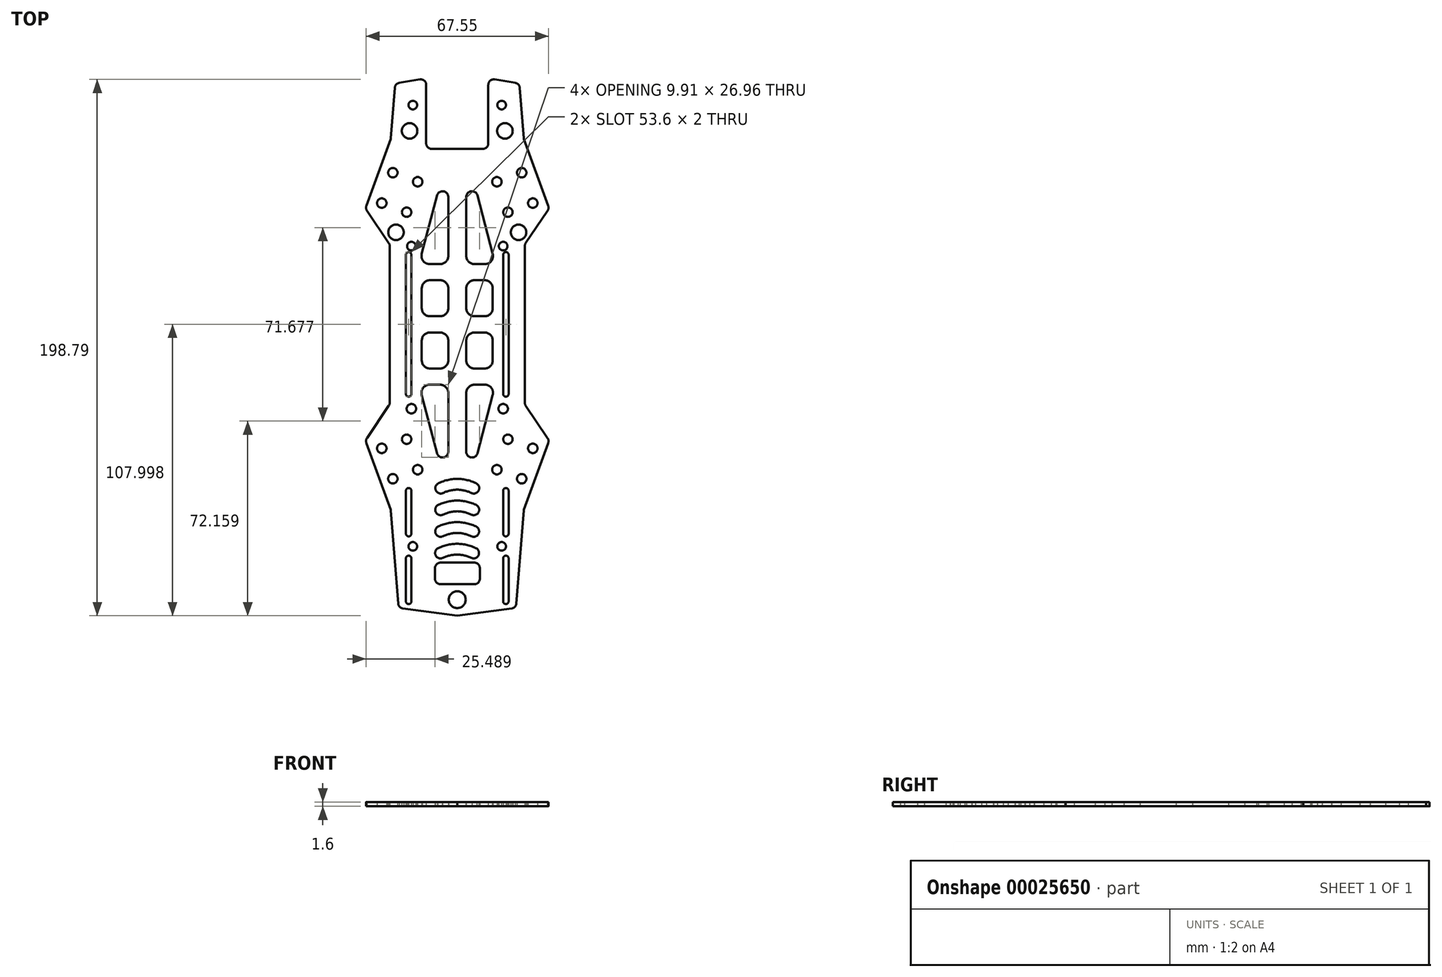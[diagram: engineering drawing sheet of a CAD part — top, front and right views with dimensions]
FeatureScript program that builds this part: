
annotation { "Feature Type Name" : "Feature", "Feature Type Description" : "" }
export const myFeature = defineFeature(function(context is Context, id is Id, definition is map)
    precondition{}
    {
        {
            var Q0;
            Q0=qCreatedBy(makeId("Top.planeOp"),FACE);
            var sketch = newSketch(context, id + "F0", { "sketchPlane" : qUnion([Q0])});
            skLineSegment(sketch, "E0.0", {"start": v(-32.77, 46.7) * mm, "end": v(-24.68, 34.7) * mm});
            skLineSegment(sketch, "E1.0", {"start": v(-24, 73.27) * mm, "end": v(-32.95, 48.59) * mm});
            skLineSegment(sketch, "E2.0", {"start": v(-22.46, 92.29) * mm, "end": v(-23.93, 73.54) * mm});
            skArc(sketch, "E3.0", {"start": v(-32.95, 48.59) * mm, "mid": v(-33.1, 47.62) * mm, "end": v(-32.77, 46.7) * mm});
            skArc(sketch, "E4.0", {"start": v(-20.81, 94.1) * mm, "mid": v(-21.94, 93.47) * mm, "end": v(-22.46, 92.29) * mm});
            skCircle(sketch, "E5.0", {"center": v(-15.79, 85.85) * mm, "radius": 1.6 * mm});
            skCircle(sketch, "E6.0", {"center": v(-14, 57.43) * mm, "radius": 1.75 * mm});
            skCircle(sketch, "E7.0", {"center": v(-14.59, 17.14) * mm, "radius": 1.5 * mm, "construction": true});
            skArc(sketch, "E8.0", {"start": v(-24.68, 34.7) * mm, "mid": v(-24.42, 34.17) * mm, "end": v(-24.34, 33.59) * mm});
            skLineSegment(sketch, "E9", {"start": v(0.66, 1.44) * mm, "end": v(0.66, -91.06) * mm, "construction": true});
            skCircle(sketch, "E10.2.MirrorC", {"center": v(15.91, 17.14) * mm, "radius": 1.5 * mm, "construction": true});
            skLineSegment(sketch, "E11", {"start": v(-20.81, 94.1) * mm, "end": v(-13.16, 95.36) * mm});
            skPoint(sketch, "E12.rect.middle", {"position": v(0.66, 1.44) * mm});
            skLineSegment(sketch, "E13", {"start": v(-23.2, 60.8) * mm, "end": v(-14, 57.43) * mm, "construction": true});
            skLineSegment(sketch, "E14", {"start": v(-14, 57.43) * mm, "end": v(-18.08, 46.19) * mm, "construction": true});
            skLineSegment(sketch, "E15", {"start": v(-18.08, 46.19) * mm, "end": v(-27.3, 49.53) * mm, "construction": true});
            skLineSegment(sketch, "E16", {"start": v(-23.2, 60.8) * mm, "end": v(-27.3, 49.53) * mm, "construction": true});
            skLineSegment(sketch, "E17", {"start": v(0.66, -91.06) * mm, "end": v(0.66, -155.3) * mm, "construction": true});
            skLineSegment(sketch, "E18.0", {"start": v(-18.34, 4.59) * mm, "end": v(-18.34, 30.39) * mm});
            skLineSegment(sketch, "E19.0", {"start": v(-16.34, 4.59) * mm, "end": v(-16.34, 30.39) * mm});
            skArc(sketch, "E20", {"start": v(-16.34, 30.39) * mm, "mid": v(-17.34, 31.39) * mm, "end": v(-18.34, 30.39) * mm});
            skArc(sketch, "E21.0.MirrorCS", {"start": v(17.66, 30.39) * mm, "mid": v(18.66, 31.39) * mm, "end": v(19.66, 30.39) * mm});
            skLineSegment(sketch, "E22.0.MirrorCS", {"start": v(19.66, 4.59) * mm, "end": v(19.66, 30.39) * mm});
            skLineSegment(sketch, "E23.0.MirrorCS", {"start": v(17.66, 4.59) * mm, "end": v(17.66, 30.39) * mm});
            skLineSegment(sketch, "E24.trimOffspring", {"start": v(-16.34, -82.12) * mm, "end": v(-16.34, -98.08) * mm});
            skLineSegment(sketch, "E25.trimOffspring", {"start": v(-18.34, -57.05) * mm, "end": v(-18.34, -72.99) * mm});
            skLineSegment(sketch, "E26.trimOffspring", {"start": v(-16.34, -57.05) * mm, "end": v(-16.34, -72.99) * mm});
            skLineSegment(sketch, "E27.0", {"start": v(-10.84, 93.38) * mm, "end": v(-10.84, 71.62) * mm});
            skArc(sketch, "E28.filletArc", {"start": v(-10.84, 93.38) * mm, "mid": v(-11.54, 94.9) * mm, "end": v(-13.16, 95.36) * mm});
            skLineSegment(sketch, "E29", {"start": v(-8.84, 69.62) * mm, "end": v(0.66, 69.62) * mm});
            skPoint(sketch, "E30.visualSharp", {"position": v(-10.84, 69.62) * mm});
            skArc(sketch, "E30.filletArc", {"start": v(-10.84, 71.62) * mm, "mid": v(-10.25, 70.2) * mm, "end": v(-8.84, 69.62) * mm});
            skCircle(sketch, "E31", {"center": v(-16.99, 76.28) * mm, "radius": 2.88 * mm});
            skCircle(sketch, "E32.0.MirrorC", {"center": v(18.31, 76.28) * mm, "radius": 2.88 * mm});
            skCircle(sketch, "E33", {"center": v(-22.04, 38.7) * mm, "radius": 2.88 * mm});
            skLineSegment(sketch, "E34", {"start": v(-24.34, 33.59) * mm, "end": v(-24.34, 4.59) * mm});
            skLineSegment(sketch, "E35", {"start": v(-24.34, 4.59) * mm, "end": v(38, 4.59) * mm, "construction": true});
            skLineSegment(sketch, "E36", {"start": v(0.66, 107.12) * mm, "end": v(0.66, 1.44) * mm, "construction": true});
            skLineSegment(sketch, "E37", {"start": v(0.66, 69.62) * mm, "end": v(0.66, 72.7) * mm, "construction": true});
            skLineSegment(sketch, "E38.0.MirrorCS", {"start": v(-24.34, -24.41) * mm, "end": v(-24.34, 4.59) * mm});
            skLineSegment(sketch, "E39.0.MirrorCS", {"start": v(19.66, 4.59) * mm, "end": v(19.66, -21.21) * mm});
            skLineSegment(sketch, "E40.0.MirrorCS", {"start": v(17.66, 4.59) * mm, "end": v(17.66, -21.21) * mm});
            skLineSegment(sketch, "E41.0.MirrorCS", {"start": v(-16.34, 4.59) * mm, "end": v(-16.34, -21.21) * mm});
            skLineSegment(sketch, "E42.0.MirrorCS", {"start": v(-18.34, 4.59) * mm, "end": v(-18.34, -21.21) * mm});
            skCircle(sketch, "E43.0.MirrorC", {"center": v(-14.59, -7.97) * mm, "radius": 1.5 * mm, "construction": true});
            skCircle(sketch, "E44.0.MirrorC", {"center": v(15.91, -7.97) * mm, "radius": 1.5 * mm, "construction": true});
            skLineSegment(sketch, "E45.0.MirrorCS", {"start": v(-32.77, -37.52) * mm, "end": v(-24.68, -25.53) * mm});
            skCircle(sketch, "E46.0.MirrorC", {"center": v(-16.34, -26.66) * mm, "radius": 1.75 * mm});
            skCircle(sketch, "E47.0.MirrorC", {"center": v(17.66, -26.66) * mm, "radius": 1.75 * mm});
            skLineSegment(sketch, "E48.0.MirrorCS", {"start": v(-24, -64.1) * mm, "end": v(-32.95, -39.41) * mm});
            skLineSegment(sketch, "E49.0.MirrorCS", {"start": v(-21.22, -98.85) * mm, "end": v(-23.93, -64.36) * mm});
            skArc(sketch, "E50.0.MirrorCS", {"start": v(-32.95, -39.41) * mm, "mid": v(-33.1, -38.44) * mm, "end": v(-32.77, -37.52) * mm});
            skPoint(sketch, "E51.orphan", {"position": v(-22.46, -83.11) * mm});
            skLineSegment(sketch, "E52", {"start": v(-19.5, -100.68) * mm, "end": v(0.66, -103.41) * mm});
            skArc(sketch, "E53", {"start": v(-16.34, -57.05) * mm, "mid": v(-17.34, -56.05) * mm, "end": v(-18.34, -57.05) * mm});
            skArc(sketch, "E54", {"start": v(-18.34, -72.99) * mm, "mid": v(-17.34, -73.99) * mm, "end": v(-16.34, -72.99) * mm});
            skLineSegment(sketch, "E55", {"start": v(-18.34, -82.12) * mm, "end": v(-18.34, -98.08) * mm});
            skArc(sketch, "E56", {"start": v(-16.34, -82.12) * mm, "mid": v(-17.34, -81.12) * mm, "end": v(-18.34, -82.12) * mm});
            skArc(sketch, "E57", {"start": v(-18.34, -98.08) * mm, "mid": v(-17.34, -99.08) * mm, "end": v(-16.34, -98.08) * mm});
            skLineSegment(sketch, "E58.0.MirrorCS", {"start": v(17.66, -57.05) * mm, "end": v(17.66, -72.99) * mm});
            skLineSegment(sketch, "E59.0.MirrorCS", {"start": v(19.66, -57.05) * mm, "end": v(19.66, -72.99) * mm});
            skArc(sketch, "E60.0.MirrorCS", {"start": v(17.66, -57.05) * mm, "mid": v(18.66, -56.05) * mm, "end": v(19.66, -57.05) * mm});
            skArc(sketch, "E61.0.MirrorCS", {"start": v(19.66, -72.99) * mm, "mid": v(18.66, -73.99) * mm, "end": v(17.66, -72.99) * mm});
            skArc(sketch, "E62.0.MirrorCS", {"start": v(17.66, -82.12) * mm, "mid": v(18.66, -81.12) * mm, "end": v(19.66, -82.12) * mm});
            skLineSegment(sketch, "E63.0.MirrorCS", {"start": v(19.66, -82.12) * mm, "end": v(19.66, -98.08) * mm});
            skLineSegment(sketch, "E64.0.MirrorCS", {"start": v(17.66, -82.12) * mm, "end": v(17.66, -98.08) * mm});
            skArc(sketch, "E65.0.MirrorCS", {"start": v(19.66, -98.08) * mm, "mid": v(18.66, -99.08) * mm, "end": v(17.66, -98.08) * mm});
            skCircle(sketch, "E66", {"center": v(0.66, -97.41) * mm, "radius": 3.12 * mm});
            skArc(sketch, "E67", {"start": v(-18.34, -21.21) * mm, "mid": v(-17.34, -22.21) * mm, "end": v(-16.34, -21.21) * mm});
            skArc(sketch, "E68", {"start": v(17.66, -21.21) * mm, "mid": v(18.66, -22.21) * mm, "end": v(19.66, -21.21) * mm});
            skPoint(sketch, "E69.visualSharp", {"position": v(-21.1, -100.46) * mm});
            skArc(sketch, "E69.filletArc", {"start": v(-21.22, -98.85) * mm, "mid": v(-20.68, -100.07) * mm, "end": v(-19.5, -100.68) * mm});
            skLineSegment(sketch, "E70.0", {"start": v(-2.66, 51.83) * mm, "end": v(-2.66, 29.95) * mm});
            skLineSegment(sketch, "E71", {"start": v(-5.66, 26.95) * mm, "end": v(-9.58, 26.95) * mm});
            skLineSegment(sketch, "E72", {"start": v(-12.48, 30.7) * mm, "end": v(-6.83, 52.34) * mm});
            skArc(sketch, "E73", {"start": v(-2.66, 51.83) * mm, "mid": v(-4.53, 53.9) * mm, "end": v(-6.83, 52.34) * mm});
            skPoint(sketch, "E74.visualSharp", {"position": v(-13.46, 26.95) * mm});
            skArc(sketch, "E74.filletArc", {"start": v(-12.48, 30.7) * mm, "mid": v(-11.95, 28.11) * mm, "end": v(-9.58, 26.95) * mm});
            skPoint(sketch, "E75.visualSharp", {"position": v(-2.66, 26.95) * mm});
            skArc(sketch, "E75.filletArc", {"start": v(-5.66, 26.95) * mm, "mid": v(-3.54, 27.83) * mm, "end": v(-2.66, 29.95) * mm});
            skArc(sketch, "E76.0.MirrorCS", {"start": v(4, 51.83) * mm, "mid": v(5.85, 53.9) * mm, "end": v(8.16, 52.34) * mm});
            skLineSegment(sketch, "E77.0.MirrorCS", {"start": v(13.8, 30.7) * mm, "end": v(8.16, 52.34) * mm});
            skLineSegment(sketch, "E78.0.MirrorCS", {"start": v(4, 51.83) * mm, "end": v(4, 29.95) * mm});
            skLineSegment(sketch, "E79.0.MirrorCS", {"start": v(7, 26.95) * mm, "end": v(10.9, 26.95) * mm});
            skArc(sketch, "E80.0.MirrorCS", {"start": v(13.8, 30.7) * mm, "mid": v(13.28, 28.11) * mm, "end": v(10.9, 26.95) * mm});
            skArc(sketch, "E81.0.MirrorCS", {"start": v(7, 26.95) * mm, "mid": v(4.87, 27.83) * mm, "end": v(4, 29.95) * mm});
            skArc(sketch, "E82.0.MirrorCS", {"start": v(4, -42.66) * mm, "mid": v(5.85, -44.73) * mm, "end": v(8.16, -43.16) * mm});
            skLineSegment(sketch, "E83.0.MirrorCS", {"start": v(4, -42.66) * mm, "end": v(4, -20.77) * mm});
            skArc(sketch, "E84.0.MirrorCS", {"start": v(7, -17.77) * mm, "mid": v(4.87, -18.65) * mm, "end": v(4, -20.77) * mm});
            skLineSegment(sketch, "E85.0.MirrorCS", {"start": v(7, -17.77) * mm, "end": v(10.9, -17.77) * mm});
            skArc(sketch, "E86.0.MirrorCS", {"start": v(13.8, -21.53) * mm, "mid": v(13.28, -18.94) * mm, "end": v(10.9, -17.77) * mm});
            skLineSegment(sketch, "E87.0.MirrorCS", {"start": v(13.8, -21.53) * mm, "end": v(8.16, -43.16) * mm});
            skArc(sketch, "E88.0.MirrorCS", {"start": v(-2.66, -42.66) * mm, "mid": v(-4.53, -44.73) * mm, "end": v(-6.83, -43.16) * mm});
            skLineSegment(sketch, "E89.0.MirrorCS", {"start": v(-2.66, -42.66) * mm, "end": v(-2.66, -20.77) * mm});
            skArc(sketch, "E90.0.MirrorCS", {"start": v(-5.66, -17.77) * mm, "mid": v(-3.54, -18.65) * mm, "end": v(-2.66, -20.77) * mm});
            skLineSegment(sketch, "E91.0.MirrorCS", {"start": v(-5.66, -17.77) * mm, "end": v(-9.58, -17.77) * mm});
            skArc(sketch, "E92.0.MirrorCS", {"start": v(-12.48, -21.53) * mm, "mid": v(-11.95, -18.94) * mm, "end": v(-9.58, -17.77) * mm});
            skLineSegment(sketch, "E93.0.MirrorCS", {"start": v(-12.48, -21.53) * mm, "end": v(-6.83, -43.16) * mm});
            skLineSegment(sketch, "E94", {"start": v(-12.84, -98.08) * mm, "end": v(0.66, -98.08) * mm, "construction": true});
            skArc(sketch, "E95.0", {"start": v(0.66, -52.66) * mm, "mid": v(-3.08, -53.13) * mm, "end": v(-6.61, -54.42) * mm});
            skArc(sketch, "E96.0.MirrorCS", {"start": v(0.66, -52.66) * mm, "mid": v(4.4, -53.13) * mm, "end": v(7.94, -54.42) * mm});
            skArc(sketch, "E97.0", {"start": v(0.66, -56.66) * mm, "mid": v(3.48, -57.02) * mm, "end": v(6.15, -58) * mm});
            skArc(sketch, "E97.1", {"start": v(0.66, -56.66) * mm, "mid": v(-2.16, -57.02) * mm, "end": v(-4.82, -58) * mm});
            skArc(sketch, "E98", {"start": v(-6.61, -54.42) * mm, "mid": v(-7.26, -56.98) * mm, "end": v(-4.82, -58) * mm});
            skArc(sketch, "E99.0.MirrorCS", {"start": v(7.94, -54.42) * mm, "mid": v(8.59, -56.98) * mm, "end": v(6.15, -58) * mm});
            skArc(sketch, "E100.1.0.0", {"start": v(0.64, -64.68) * mm, "mid": v(-2.18, -65.04) * mm, "end": v(-4.85, -66.02) * mm});
            skArc(sketch, "E100.1.0.1", {"start": v(-6.64, -62.45) * mm, "mid": v(-7.28, -65) * mm, "end": v(-4.85, -66.02) * mm});
            skArc(sketch, "E100.1.0.2", {"start": v(0.64, -60.68) * mm, "mid": v(-3.1, -61.15) * mm, "end": v(-6.64, -62.45) * mm});
            skArc(sketch, "E100.1.0.3", {"start": v(0.64, -60.68) * mm, "mid": v(4.38, -61.15) * mm, "end": v(7.92, -62.45) * mm});
            skArc(sketch, "E100.1.0.4", {"start": v(7.92, -62.45) * mm, "mid": v(8.56, -65) * mm, "end": v(6.13, -66.02) * mm});
            skArc(sketch, "E100.1.0.5", {"start": v(0.64, -64.68) * mm, "mid": v(3.46, -65.04) * mm, "end": v(6.13, -66.02) * mm});
            skArc(sketch, "E100.2.0.0", {"start": v(0.62, -72.7) * mm, "mid": v(-2.2, -73.06) * mm, "end": v(-4.87, -74.04) * mm});
            skArc(sketch, "E100.2.0.1", {"start": v(-6.66, -70.47) * mm, "mid": v(-7.3, -73.03) * mm, "end": v(-4.87, -74.04) * mm});
            skArc(sketch, "E100.2.0.2", {"start": v(0.62, -68.7) * mm, "mid": v(-3.12, -69.17) * mm, "end": v(-6.66, -70.47) * mm});
            skArc(sketch, "E100.2.0.3", {"start": v(0.62, -68.7) * mm, "mid": v(4.35, -69.17) * mm, "end": v(7.9, -70.47) * mm});
            skArc(sketch, "E100.2.0.4", {"start": v(7.9, -70.47) * mm, "mid": v(8.54, -73.03) * mm, "end": v(6.1, -74.04) * mm});
            skArc(sketch, "E100.2.0.5", {"start": v(0.62, -72.7) * mm, "mid": v(3.43, -73.06) * mm, "end": v(6.1, -74.04) * mm});
            skArc(sketch, "E100.3.0.0", {"start": v(0.6, -80.72) * mm, "mid": v(-2.23, -81.09) * mm, "end": v(-4.9, -82.07) * mm});
            skArc(sketch, "E100.3.0.1", {"start": v(-6.69, -78.49) * mm, "mid": v(-7.33, -81.05) * mm, "end": v(-4.9, -82.07) * mm});
            skArc(sketch, "E100.3.0.2", {"start": v(0.6, -76.72) * mm, "mid": v(-3.15, -77.2) * mm, "end": v(-6.69, -78.49) * mm});
            skArc(sketch, "E100.3.0.3", {"start": v(0.6, -76.72) * mm, "mid": v(4.33, -77.2) * mm, "end": v(7.87, -78.49) * mm});
            skArc(sketch, "E100.3.0.4", {"start": v(7.87, -78.49) * mm, "mid": v(8.51, -81.05) * mm, "end": v(6.08, -82.07) * mm});
            skArc(sketch, "E100.3.0.5", {"start": v(0.6, -80.72) * mm, "mid": v(3.41, -81.09) * mm, "end": v(6.08, -82.07) * mm});
            skLineSegment(sketch, "E100.direction1", {"start": v(0.87, -69.38) * mm, "end": v(0.85, -77.4) * mm, "construction": true});
            skCircle(sketch, "E101.0.MirrorC", {"center": v(-23.2, 59.97) * mm, "radius": 1.5 * mm, "construction": true});
            skCircle(sketch, "E101.3.MirrorC", {"center": v(-27.3, 49.53) * mm, "radius": 1.5 * mm, "construction": true});
            skCircle(sketch, "E102", {"center": v(-23.2, 60.8) * mm, "radius": 1.75 * mm});
            skCircle(sketch, "E103", {"center": v(-27.3, 49.53) * mm, "radius": 1.75 * mm});
            skCircle(sketch, "E104", {"center": v(-18.1, 46.15) * mm, "radius": 1.75 * mm});
            skCircle(sketch, "E105.0.MirrorC", {"center": v(24.53, 60.8) * mm, "radius": 1.75 * mm});
            skCircle(sketch, "E106.0.MirrorC", {"center": v(15.33, 57.43) * mm, "radius": 1.75 * mm});
            skCircle(sketch, "E107.0.MirrorC", {"center": v(19.42, 46.15) * mm, "radius": 1.75 * mm});
            skCircle(sketch, "E108.0.MirrorC", {"center": v(28.62, 49.53) * mm, "radius": 1.75 * mm});
            skCircle(sketch, "E109.0.MirrorC", {"center": v(23.36, 38.7) * mm, "radius": 2.88 * mm});
            skArc(sketch, "E110.0.MirrorCS", {"start": v(12.16, 93.38) * mm, "mid": v(12.87, 94.9) * mm, "end": v(14.49, 95.36) * mm});
            skLineSegment(sketch, "E111.0.MirrorCS", {"start": v(12.16, 93.38) * mm, "end": v(12.16, 71.62) * mm});
            skLineSegment(sketch, "E112.0.MirrorCS", {"start": v(10.16, 69.62) * mm, "end": v(0.66, 69.62) * mm});
            skPoint(sketch, "E113.0.MirrorP", {"position": v(12.16, 69.62) * mm});
            skLineSegment(sketch, "E114.0.MirrorCS", {"start": v(22.14, 94.1) * mm, "end": v(14.49, 95.36) * mm});
            skArc(sketch, "E115.0.MirrorCS", {"start": v(22.14, 94.1) * mm, "mid": v(23.27, 93.47) * mm, "end": v(23.79, 92.29) * mm});
            skPoint(sketch, "E116.newPointB", {"position": v(-23.94, 73.4) * mm});
            skArc(sketch, "E116.filletArc", {"start": v(-24, 73.27) * mm, "mid": v(-23.95, 73.4) * mm, "end": v(-23.93, 73.54) * mm});
            skLineSegment(sketch, "E117.0.MirrorCS", {"start": v(23.79, 92.29) * mm, "end": v(25.26, 73.54) * mm});
            skArc(sketch, "E118.0.MirrorCS", {"start": v(25.32, 73.27) * mm, "mid": v(25.28, 73.4) * mm, "end": v(25.26, 73.54) * mm});
            skLineSegment(sketch, "E119.0.MirrorCS", {"start": v(25.32, 73.27) * mm, "end": v(34.28, 48.59) * mm});
            skArc(sketch, "E120.0.MirrorCS", {"start": v(34.28, 48.59) * mm, "mid": v(34.43, 47.62) * mm, "end": v(34.1, 46.7) * mm});
            skLineSegment(sketch, "E121.0.MirrorCS", {"start": v(34.1, 46.7) * mm, "end": v(26, 34.7) * mm});
            skArc(sketch, "E122.0.MirrorCS", {"start": v(26, 34.7) * mm, "mid": v(25.75, 34.17) * mm, "end": v(25.66, 33.59) * mm});
            skLineSegment(sketch, "E123.0.MirrorCS", {"start": v(25.66, 33.59) * mm, "end": v(25.66, 4.59) * mm});
            skLineSegment(sketch, "E124.0.MirrorCS", {"start": v(25.66, -24.41) * mm, "end": v(25.66, 4.59) * mm});
            skArc(sketch, "E125", {"start": v(-24.68, -25.53) * mm, "mid": v(-24.42, -25) * mm, "end": v(-24.34, -24.41) * mm});
            skArc(sketch, "E126.0.MirrorCS", {"start": v(26, -25.53) * mm, "mid": v(25.75, -25) * mm, "end": v(25.66, -24.41) * mm});
            skLineSegment(sketch, "E127.0.MirrorCS", {"start": v(34.1, -37.52) * mm, "end": v(26, -25.53) * mm});
            skArc(sketch, "E128.0.MirrorCS", {"start": v(34.28, -39.41) * mm, "mid": v(34.43, -38.44) * mm, "end": v(34.1, -37.52) * mm});
            skLineSegment(sketch, "E129.0.MirrorCS", {"start": v(25.27, -64.23) * mm, "end": v(34.28, -39.41) * mm});
            skPoint(sketch, "E130.newPointA", {"position": v(-23.94, -64.23) * mm});
            skArc(sketch, "E130.filletArc", {"start": v(-23.93, -64.36) * mm, "mid": v(-23.95, -64.23) * mm, "end": v(-24, -64.1) * mm});
            skArc(sketch, "E131.0.MirrorCS", {"start": v(25.26, -64.36) * mm, "mid": v(25.28, -64.23) * mm, "end": v(25.32, -64.1) * mm});
            skLineSegment(sketch, "E132.0.MirrorCS", {"start": v(22.55, -98.85) * mm, "end": v(25.26, -64.36) * mm});
            skArc(sketch, "E133.0.MirrorCS", {"start": v(22.55, -98.85) * mm, "mid": v(22, -100.07) * mm, "end": v(20.82, -100.68) * mm});
            skLineSegment(sketch, "E134.0.MirrorCS", {"start": v(20.82, -100.68) * mm, "end": v(0.66, -103.41) * mm});
            skArc(sketch, "E135.0.MirrorCS", {"start": v(12.16, 71.62) * mm, "mid": v(11.58, 70.2) * mm, "end": v(10.16, 69.62) * mm});
            skLineSegment(sketch, "E136", {"start": v(-2.66, 29.95) * mm, "end": v(-2.66, 4.59) * mm, "construction": true});
            skLineSegment(sketch, "E137.0", {"start": v(-5.66, 20.95) * mm, "end": v(-9.48, 20.95) * mm});
            skLineSegment(sketch, "E138.trimOffspring", {"start": v(-12.48, 17.95) * mm, "end": v(-12.48, 10.59) * mm});
            skLineSegment(sketch, "E139.trimOffspring", {"start": v(-9.48, 7.59) * mm, "end": v(-5.66, 7.59) * mm});
            skLineSegment(sketch, "E140", {"start": v(-2.66, 10.59) * mm, "end": v(-2.66, 17.95) * mm});
            skPoint(sketch, "E141.visualSharp", {"position": v(-12.48, 20.95) * mm});
            skArc(sketch, "E141.filletArc", {"start": v(-9.48, 20.95) * mm, "mid": v(-11.6, 20.07) * mm, "end": v(-12.48, 17.95) * mm});
            skPoint(sketch, "E142.visualSharp", {"position": v(-2.66, 20.95) * mm});
            skArc(sketch, "E142.filletArc", {"start": v(-2.66, 17.95) * mm, "mid": v(-3.54, 20.07) * mm, "end": v(-5.66, 20.95) * mm});
            skPoint(sketch, "E143.visualSharp", {"position": v(-12.48, 7.59) * mm});
            skArc(sketch, "E143.filletArc", {"start": v(-12.48, 10.59) * mm, "mid": v(-11.6, 8.47) * mm, "end": v(-9.48, 7.59) * mm});
            skPoint(sketch, "E144.visualSharp", {"position": v(-2.66, 7.59) * mm});
            skArc(sketch, "E144.filletArc", {"start": v(-5.66, 7.59) * mm, "mid": v(-3.54, 8.47) * mm, "end": v(-2.66, 10.59) * mm});
            skLineSegment(sketch, "E145.0.MirrorCS", {"start": v(7, 20.95) * mm, "end": v(10.8, 20.95) * mm});
            skArc(sketch, "E146.0.MirrorCS", {"start": v(4, 17.95) * mm, "mid": v(4.87, 20.07) * mm, "end": v(7, 20.95) * mm});
            skArc(sketch, "E147.0.MirrorCS", {"start": v(10.8, 20.95) * mm, "mid": v(12.93, 20.07) * mm, "end": v(13.8, 17.95) * mm});
            skLineSegment(sketch, "E148.0.MirrorCS", {"start": v(13.8, 17.95) * mm, "end": v(13.8, 10.59) * mm});
            skArc(sketch, "E149.0.MirrorCS", {"start": v(13.8, 10.59) * mm, "mid": v(12.93, 8.47) * mm, "end": v(10.8, 7.59) * mm});
            skLineSegment(sketch, "E150.0.MirrorCS", {"start": v(10.8, 7.59) * mm, "end": v(7, 7.59) * mm});
            skArc(sketch, "E151.0.MirrorCS", {"start": v(7, 7.59) * mm, "mid": v(4.87, 8.47) * mm, "end": v(4, 10.59) * mm});
            skLineSegment(sketch, "E152.0.MirrorCS", {"start": v(4, 10.59) * mm, "end": v(4, 17.95) * mm});
            skLineSegment(sketch, "E153.0.MirrorCS", {"start": v(-5.66, -11.77) * mm, "end": v(-9.48, -11.77) * mm});
            skArc(sketch, "E154.0.MirrorCS", {"start": v(-9.48, -11.77) * mm, "mid": v(-11.6, -10.9) * mm, "end": v(-12.48, -8.77) * mm});
            skLineSegment(sketch, "E155.0.MirrorCS", {"start": v(-12.48, -8.77) * mm, "end": v(-12.48, -1.41) * mm});
            skArc(sketch, "E156.0.MirrorCS", {"start": v(-12.48, -1.41) * mm, "mid": v(-11.6, 0.7) * mm, "end": v(-9.48, 1.59) * mm});
            skLineSegment(sketch, "E157.0.MirrorCS", {"start": v(-9.48, 1.59) * mm, "end": v(-5.66, 1.59) * mm});
            skArc(sketch, "E158.0.MirrorCS", {"start": v(-5.66, 1.59) * mm, "mid": v(-3.54, 0.7) * mm, "end": v(-2.66, -1.41) * mm});
            skLineSegment(sketch, "E159.0.MirrorCS", {"start": v(-2.66, -1.41) * mm, "end": v(-2.66, -8.77) * mm});
            skArc(sketch, "E160.0.MirrorCS", {"start": v(-2.66, -8.77) * mm, "mid": v(-3.54, -10.9) * mm, "end": v(-5.66, -11.77) * mm});
            skArc(sketch, "E161.0.MirrorCS", {"start": v(4, -8.77) * mm, "mid": v(4.87, -10.9) * mm, "end": v(7, -11.77) * mm});
            skLineSegment(sketch, "E162.0.MirrorCS", {"start": v(4, -1.41) * mm, "end": v(4, -8.77) * mm});
            skArc(sketch, "E163.0.MirrorCS", {"start": v(7, 1.59) * mm, "mid": v(4.87, 0.7) * mm, "end": v(4, -1.41) * mm});
            skLineSegment(sketch, "E164.0.MirrorCS", {"start": v(10.8, 1.59) * mm, "end": v(7, 1.59) * mm});
            skArc(sketch, "E165.0.MirrorCS", {"start": v(13.8, -1.41) * mm, "mid": v(12.93, 0.7) * mm, "end": v(10.8, 1.59) * mm});
            skLineSegment(sketch, "E166.0.MirrorCS", {"start": v(13.8, -8.77) * mm, "end": v(13.8, -1.41) * mm});
            skArc(sketch, "E167.0.MirrorCS", {"start": v(10.8, -11.77) * mm, "mid": v(12.93, -10.9) * mm, "end": v(13.8, -8.77) * mm});
            skLineSegment(sketch, "E168.0.MirrorCS", {"start": v(7, -11.77) * mm, "end": v(10.8, -11.77) * mm});
            skCircle(sketch, "E169.0.MirrorC", {"center": v(17.11, 85.85) * mm, "radius": 1.6 * mm});
            skLineSegment(sketch, "E170", {"start": v(-16.34, 35.84) * mm, "end": v(-16.34, 32.79) * mm, "construction": true});
            skLineSegment(sketch, "E171", {"start": v(-24.34, 33.59) * mm, "end": v(-16.34, 33.59) * mm, "construction": true});
            skCircle(sketch, "E172", {"center": v(-16.34, 33.59) * mm, "radius": 1.6 * mm});
            skCircle(sketch, "E173.0.MirrorC", {"center": v(17.66, 33.59) * mm, "radius": 1.6 * mm});
            skLineSegment(sketch, "E174", {"start": v(25.66, 33.59) * mm, "end": v(17.66, 33.59) * mm, "construction": true});
            skCircle(sketch, "E175", {"center": v(-15.78, -77.67) * mm, "radius": 1.6 * mm});
            skCircle(sketch, "E176.0.MirrorC", {"center": v(17.1, -77.67) * mm, "radius": 1.6 * mm});
            skPoint(sketch, "E177.rect.middle", {"position": v(0.66, -86.57) * mm});
            skLineSegment(sketch, "E178.rect.bottom", {"start": v(7.01, -91.72) * mm, "end": v(-5.58, -91.72) * mm});
            skLineSegment(sketch, "E178.rect.top", {"start": v(7.01, -83.72) * mm, "end": v(-5.58, -83.72) * mm});
            skLineSegment(sketch, "E178.rect.left", {"start": v(9.01, -89.72) * mm, "end": v(9.01, -85.72) * mm});
            skLineSegment(sketch, "E178.rect.right", {"start": v(-7.58, -89.72) * mm, "end": v(-7.58, -85.72) * mm});
            skPoint(sketch, "E178.rect.middle", {"position": v(0.72, -87.72) * mm});
            skPoint(sketch, "E179.visualSharp", {"position": v(-7.58, -83.72) * mm});
            skArc(sketch, "E179.filletArc", {"start": v(-5.58, -83.72) * mm, "mid": v(-7, -84.3) * mm, "end": v(-7.58, -85.72) * mm});
            skPoint(sketch, "E180.visualSharp", {"position": v(9.01, -83.72) * mm});
            skArc(sketch, "E180.filletArc", {"start": v(9.01, -85.72) * mm, "mid": v(8.43, -84.3) * mm, "end": v(7.01, -83.72) * mm});
            skPoint(sketch, "E181.visualSharp", {"position": v(-7.58, -91.72) * mm});
            skArc(sketch, "E181.filletArc", {"start": v(-7.58, -89.72) * mm, "mid": v(-7, -91.14) * mm, "end": v(-5.58, -91.72) * mm});
            skPoint(sketch, "E182.visualSharp", {"position": v(9.01, -91.72) * mm});
            skArc(sketch, "E182.filletArc", {"start": v(7.01, -91.72) * mm, "mid": v(8.43, -91.14) * mm, "end": v(9.01, -89.72) * mm});
            skCircle(sketch, "E183", {"center": v(-18.1, -37.98) * mm, "radius": 1.75 * mm});
            skCircle(sketch, "E184", {"center": v(-27.3, -41.35) * mm, "radius": 1.75 * mm});
            skCircle(sketch, "E185", {"center": v(-23.2, -52.63) * mm, "radius": 1.75 * mm});
            skCircle(sketch, "E186", {"center": v(-14, -49.26) * mm, "radius": 1.75 * mm});
            skCircle(sketch, "E187.0.MirrorC", {"center": v(19.42, -37.98) * mm, "radius": 1.75 * mm});
            skCircle(sketch, "E188.0.MirrorC", {"center": v(28.62, -41.35) * mm, "radius": 1.75 * mm});
            skCircle(sketch, "E189.0.MirrorC", {"center": v(24.53, -52.63) * mm, "radius": 1.75 * mm});
            skCircle(sketch, "E190.0.MirrorC", {"center": v(15.33, -49.26) * mm, "radius": 1.75 * mm});
            skSolve(sketch);
        }
        {
            var Q0;
            Q0=makeQuery(id+"F0.imprint","IMPRINT",FACE,{"disambiguationData":[TD([[makeQuery(id+"F0.imprint","IMPRINT",EDGE,{"derivedFrom":sQuery(id+"F0.wireOp",EDGE,"E0.0")}),1.0]])]});
            extrude(context, id + "F1", {"entities" : qUnion([Q0]), "depth" : 1.6 * mm});
        }
    });
